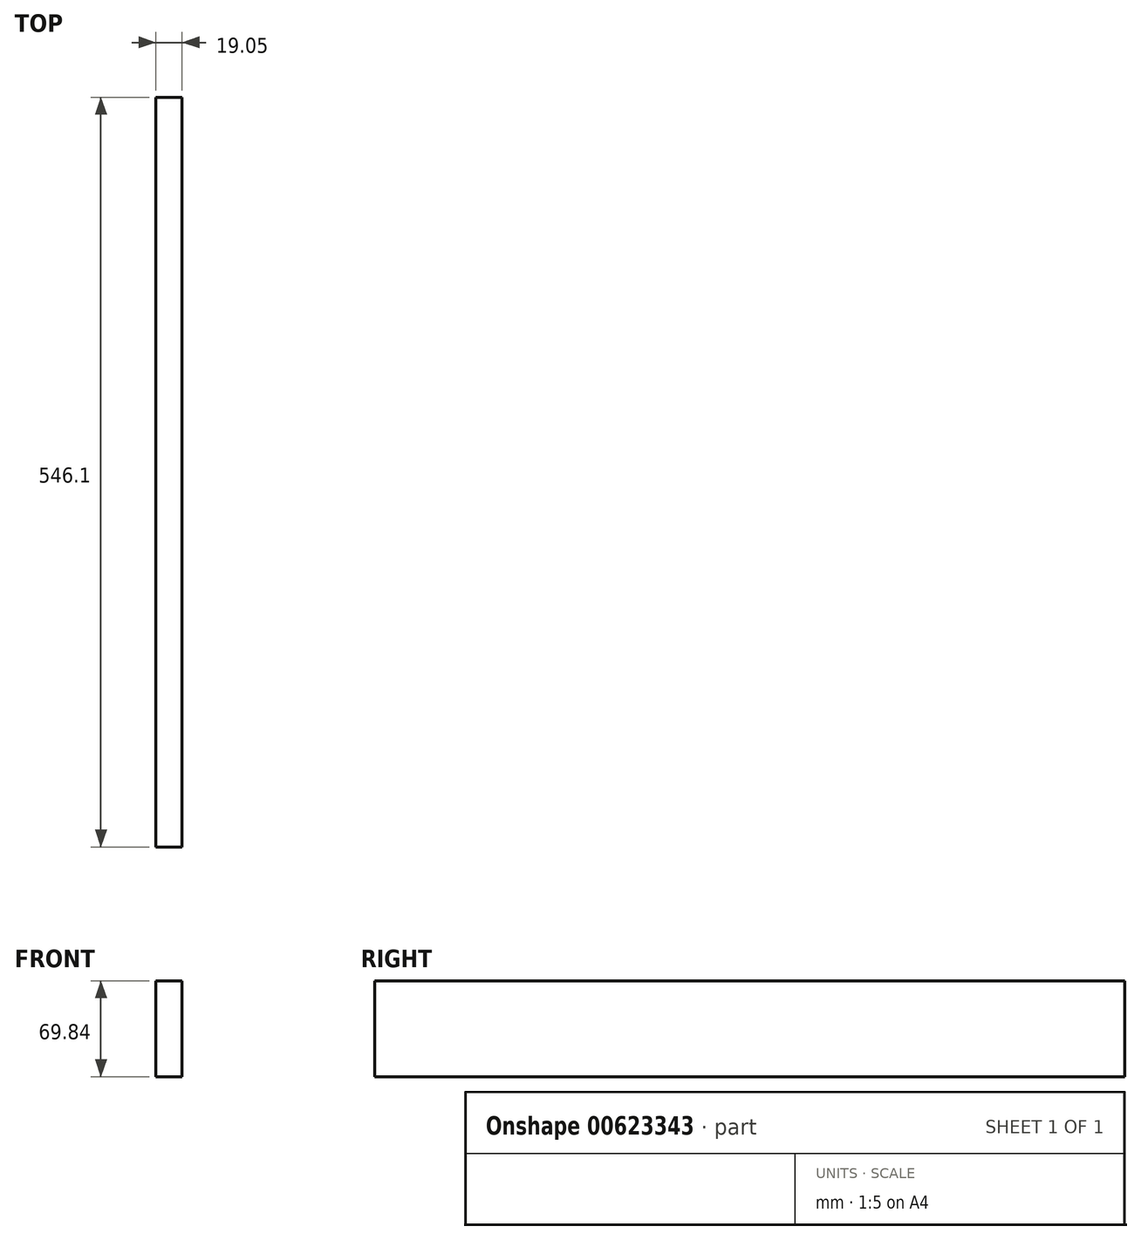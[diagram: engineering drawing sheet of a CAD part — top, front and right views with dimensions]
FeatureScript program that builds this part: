
annotation { "Feature Type Name" : "Feature", "Feature Type Description" : "" }
export const myFeature = defineFeature(function(context is Context, id is Id, definition is map)
    precondition{}
    {
        {
            var Q0;
            Q0=qCreatedBy(makeId("Right.planeOp"),FACE);
            var sketch = newSketch(context, id + "F0", { "sketchPlane" : qUnion([Q0])});
            skLineSegment(sketch, "E0.bottom", {"start": v(-273.05, 34.93) * mm, "end": v(273.05, 34.93) * mm});
            skLineSegment(sketch, "E0.top", {"start": v(-273.05, -34.93) * mm, "end": v(273.05, -34.93) * mm});
            skLineSegment(sketch, "E0.left", {"start": v(-273.05, 34.93) * mm, "end": v(-273.05, -34.93) * mm});
            skLineSegment(sketch, "E0.right", {"start": v(273.05, 34.93) * mm, "end": v(273.05, -34.93) * mm});
            skPoint(sketch, "E0.middle", {"position": v(0, 0) * mm});
            skSolve(sketch);
        }
        {
            var Q0;
            Q0=makeQuery(id+"F0.imprint","IMPRINT",FACE,{"disambiguationData":[TD([[makeQuery(id+"F0.imprint","IMPRINT",EDGE,{"derivedFrom":sQuery(id+"F0.wireOp",EDGE,"E0.bottom")}),-1.0]])]});
            extrude(context, id + "F1", {"entities" : qUnion([Q0]), "depth" : 19.05 * mm, "offsetDistance" : 25.4 * mm});
        }
    });
